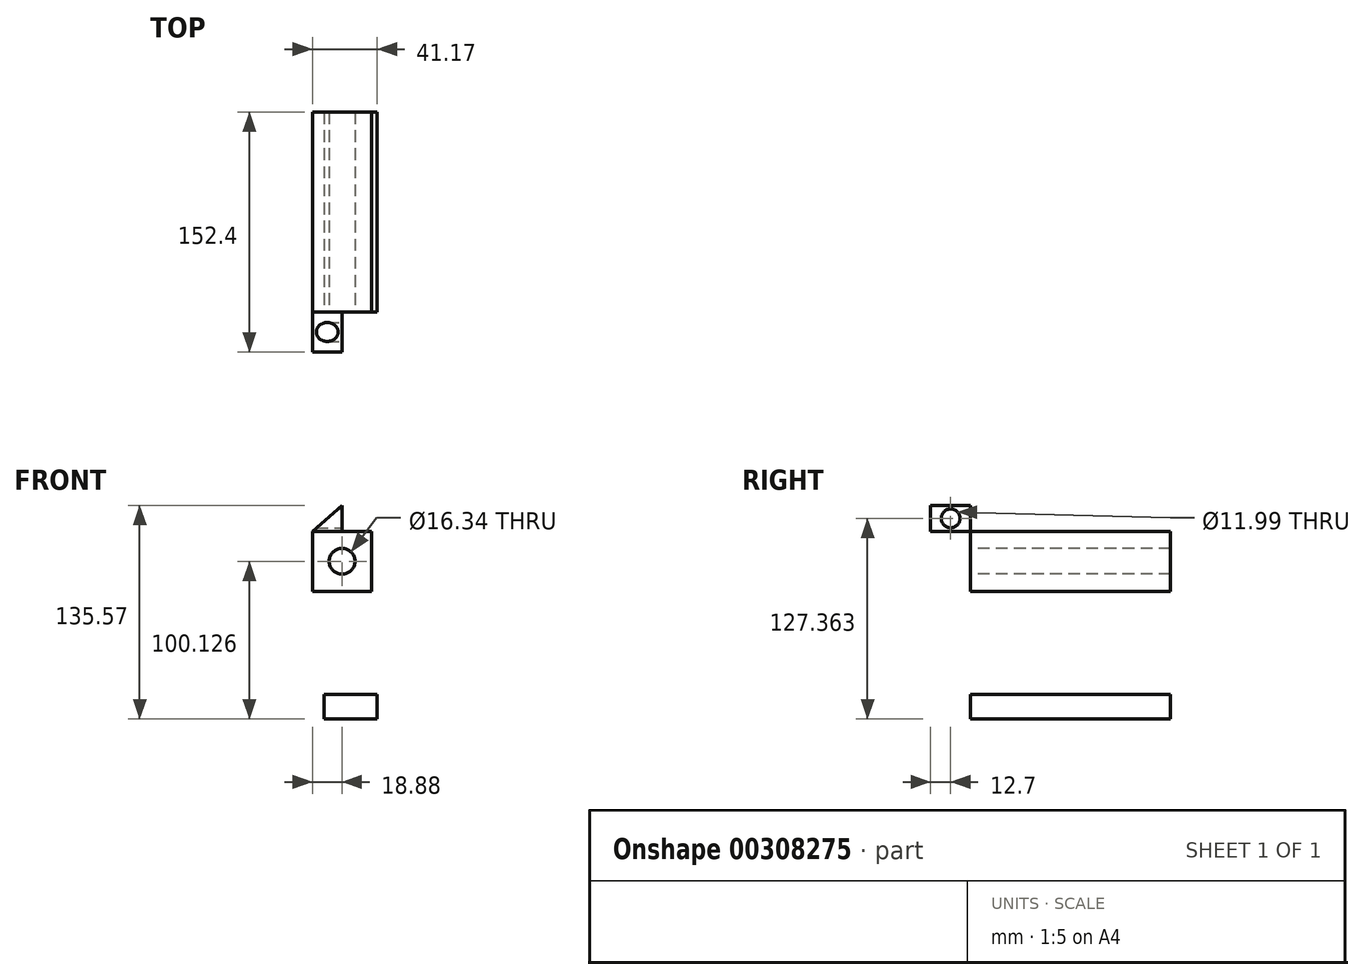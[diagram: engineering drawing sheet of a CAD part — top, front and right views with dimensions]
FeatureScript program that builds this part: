
annotation { "Feature Type Name" : "Feature", "Feature Type Description" : "" }
export const myFeature = defineFeature(function(context is Context, id is Id, definition is map)
    precondition{}
    {
        {
            var Q0;
            Q0=qCreatedBy(makeId("Front.planeOp"),FACE);
            var sketch = newSketch(context, id + "F0", { "sketchPlane" : qUnion([Q0])});
            skLineSegment(sketch, "E0", {"start": v(-49.83, -49.99) * mm, "end": v(-16.1, -49.99) * mm});
            skLineSegment(sketch, "E1", {"start": v(-16.1, -49.99) * mm, "end": v(-16.1, -65.46) * mm});
            skLineSegment(sketch, "E2", {"start": v(-16.1, -65.46) * mm, "end": v(-49.83, -65.46) * mm});
            skLineSegment(sketch, "E3", {"start": v(-49.83, -65.46) * mm, "end": v(-49.83, -49.99) * mm});
            skLineSegment(sketch, "E4", {"start": v(-57.26, 53.7) * mm, "end": v(-57.26, 15.63) * mm});
            skLineSegment(sketch, "E5", {"start": v(-57.26, 15.63) * mm, "end": v(-19.5, 15.63) * mm});
            skLineSegment(sketch, "E6", {"start": v(-19.5, 15.63) * mm, "end": v(-19.5, 53.7) * mm});
            skLineSegment(sketch, "E7", {"start": v(-57.26, 53.7) * mm, "end": v(-19.5, 53.7) * mm});
            skSolve(sketch);
        }
        {
            var Q0;
            Q0 = qSketchRegion(id + "F0", true);
            extrude(context, id + "F1", {"entities" : qUnion([Q0]), "oppositeDirection" : true, "depth" : 127 * mm});
        }
        {
            var Q0;
            Q0=makeQuery(id+"F1.opExtrude","CAP_FACE",FACE,{"disambiguationData":[OSD([sQuery(id+"F0.wireOp",EDGE,"E4"),sQuery(id+"F0.wireOp",EDGE,"E5"),sQuery(id+"F0.wireOp",EDGE,"E6"),sQuery(id+"F0.wireOp",EDGE,"E7")])],"isStart":true});
            var sketch = newSketch(context, id + "F2", { "sketchPlane" : qUnion([Q0])});
            skCircle(sketch, "E8", {"center": v(-38.38, 34.67) * mm, "radius": 8.17 * mm});
            skPoint(sketch, "E8.centerSnap0", {"position": v(-57.26, 34.67) * mm});
            skPoint(sketch, "E8.centerSnap1", {"position": v(-38.38, 53.7) * mm});
            skSolve(sketch);
        }
        {
            var Q0;
            Q0=makeQuery(id+"F2.imprint","IMPRINT",FACE,{"disambiguationData":[TD([[makeQuery(id+"F2.imprint","IMPRINT",EDGE,{"derivedFrom":sQuery(id+"F2.wireOp",EDGE,"E8")}),1.0]])]});
            extrude(context, id + "F3", {"entities" : qUnion([Q0]), "operationType" : NewBodyOperationType.REMOVE, "endBound" : BoundingType.THROUGH_ALL, "oppositeDirection" : true, "depth" : 126.24 * mm});
        }
        {
            var Q0;
            Q0=makeQuery(id+"F1.opExtrude","CAP_FACE",FACE,{"disambiguationData":[OSD([sQuery(id+"F0.wireOp",EDGE,"E4"),sQuery(id+"F0.wireOp",EDGE,"E5"),sQuery(id+"F0.wireOp",EDGE,"E6"),sQuery(id+"F0.wireOp",EDGE,"E7")])],"isStart":true});
            var sketch = newSketch(context, id + "F4", { "sketchPlane" : qUnion([Q0])});
            skLineSegment(sketch, "E9", {"start": v(-38.38, 53.7) * mm, "end": v(-38.38, 70.1) * mm});
            skPoint(sketch, "E9.endSnap0", {"position": v(-38.38, 53.7) * mm});
            skLineSegment(sketch, "E10", {"start": v(-38.38, 70.1) * mm, "end": v(-57.26, 53.7) * mm});
            skSolve(sketch);
        }
        {
            var Q0;
            Q0 = qSketchRegion(id + "F4", true);
            var Q1;
            {var subQ0=sQuery(id+"F4.wireOp",EDGE,"E9");Q1=makeQuery(id+"F4.imprint","IMPRINT",FACE,{"disambiguationData":[TD([[makeQuery(id+"F4.imprint","IMPRINT",EDGE,{"derivedFrom":subQ0}),1.0]])]});}
            extrude(context, id + "F5", {"entities" : qUnion([Q0, Q1]), "depth" : 25.4 * mm});
        }
        {
            var Q0;
            Q0=makeQuery(id+"F5.opExtrude","SWEPT_FACE",FACE,{"disambiguationData":[OSD([sQuery(id+"F4.wireOp",EDGE,"E9")])]});
            var sketch = newSketch(context, id + "F6", { "sketchPlane" : qUnion([Q0])});
            skCircle(sketch, "E11", {"center": v(-12.7, 61.9) * mm, "radius": 6 * mm});
            skPoint(sketch, "E11.centerSnap0", {"position": v(-12.7, 70.1) * mm});
            skPoint(sketch, "E11.centerSnap1", {"position": v(-25.4, 61.9) * mm});
            skSolve(sketch);
        }
        {
            var Q0;
            Q0=makeQuery(id+"F6.imprint","IMPRINT",FACE,{"disambiguationData":[TD([[makeQuery(id+"F6.imprint","IMPRINT",EDGE,{"derivedFrom":sQuery(id+"F6.wireOp",EDGE,"E11")}),1.0]])]});
            var sketch = newSketch(context, id + "F7", { "sketchPlane" : qUnion([Q0])});
            skSolve(sketch);
        }
        {
            var Q0;
            Q0 = qSketchRegion(id + "F7", true);
            var Q1;
            Q1=makeQuery(id+"F6.imprint","IMPRINT",FACE,{"disambiguationData":[TD([[makeQuery(id+"F6.imprint","IMPRINT",EDGE,{"derivedFrom":sQuery(id+"F6.wireOp",EDGE,"E11")}),1.0]])]});
            extrude(context, id + "F8", {"entities" : qUnion([Q0, Q1]), "operationType" : NewBodyOperationType.REMOVE, "oppositeDirection" : true, "depth" : 25.4 * mm});
        }
    });
